# Revit family: ANAESTIVAC 2
name_source: partatom
category: Equipement de génie climatique
revit_build: Autodesk Revit 2018 (Build: 20170223_1515(x64)
units: mm (PartAtom-declared; Revit-internal decimal feet)

## family parameters
Basée sur le plan de construction = Non
Classification = Aucun
Cote de connecteur circulaire = Utiliser le diamètre
Couper avec des vides une fois chargée = Non
Partagée = Non
Point de calcul de pièce = Non
Toujours verticalement = Oui
Type d'élément = Normal

## types (4) — shared parameters
BRANCHEMENT_TERRE = Oui
COFFRET ELEC = COFFRET ELEC STANDARD PM2 : COFFRET MIL 600x300x300
COS_PHI = 0.9
COUPE ASPI LARG = 86.3 mm
DOUBLE_ALIMENTATION = Non
NBR_POLES = 3
NEUTRE = Oui
TENSION_ALIM = 400 V
Zone de maintenance 1 = Oui
Zone de maintenance coffret = Oui
zero-valued in all types: HAUTEUR, LARGEUR, LONGUEUR

## per-type parameters (varying)
| type | CHASSIS_ASPI_LARG | COUPE REFOULEMENT | DEBIT_ASPI_VIDE | DEBIT_REFOUL_VIDE | DEPLACEMENT ASPI DROITE | DEPLACEMENT ASPI GAUCHE | DEPLACEMENT ASPI REOULEMENT HAUTEUR | DEPLACEMENT REFOULEMENT DROITE | DEPLACEMENT REFOULEMENT GAUCHE | DESCR_ALIM_X | DESCR_ASPI | DESCR_REFOUL | DIAM_ASPI_AIR | DIAM_REFOUL_VIDE | NIVEAU_SONORE(dB(A)) | POIDS(Kg) | POMPES | POMPES_LARG | POMPES_LONG | PUISS_APPARENTE | PUISS_ELECT | SUPPORT POMPES |
| Y006V | 58.3 mm | 70 mm  [stored 0.229659 ft] | 150.0 m³/h | 75.0 m³/h | 65 mm  [stored 0.213255 ft] | 165 mm | 288 mm  [stored 0.944882 ft] | 165 mm | 65 mm  [stored 0.213255 ft] | Alimentation électrique, 5G1.5mm² | Aspiration Vide; 150m3/h; G1"1/4"FEM | Refoulement Vide; 75m3/h; Ø44 | 32 mm  [stored 0.104987 ft] | 44 mm  [stored 0.144357 ft] | 61 | 110 mm  [stored 0.360892 ft] | PAV_ANAESTIVAC 2 : Y006V | 572 mm | 199 mm  [stored 0.652887 ft] | 844 VA | 1 kW | SUPPORT ANAESTIVAC 2 : Y006V - Y011V |
| Y011V | 80 mm  [stored 0.262467 ft] | 70 mm  [stored 0.229659 ft] | 288.0 m³/h | 144.0 m³/h | 70 mm  [stored 0.229659 ft] | 185 mm  [stored 0.606955 ft] | 296 mm  [stored 0.971129 ft] | 185 mm  [stored 0.606955 ft] | 70 mm  [stored 0.229659 ft] | Alimentation électrique, 5G2.5mm² | Aspiration Vide; 288m3/h; G1"1/2"FEM | Refoulement Vide; 144m3/h; Ø44 | 40 mm  [stored 0.131234 ft] | 44 mm  [stored 0.144357 ft] | 67 | 120 mm  [stored 0.393701 ft] | PAV_ANAESTIVAC 2 : Y011V | 572 mm | 199 mm  [stored 0.652887 ft] | 2000 VA | 2 kW | SUPPORT ANAESTIVAC 2 : Y006V - Y011V |
| Y020V | 58.3 mm | 90 mm  [stored 0.295276 ft] | 420.0 m³/h | 210.0 m³/h | 87.5 mm  [stored 0.287073 ft] | 207.5 mm  [stored 0.680774 ft] | 298 mm  [stored 0.97769 ft] | 207.5 mm  [stored 0.680774 ft] | 87.5 mm  [stored 0.287073 ft] | Alimentation électrique, 5G4mm² | Aspiration Vide; 420m3/h; G2"FEM | Refoulement Vide; 210m3/h; Ø60 | 50 mm  [stored 0.164042 ft] | 60 mm  [stored 0.19685 ft] | 71 | 140 mm  [stored 0.459318 ft] | PAV_ANAESTIVAC 2 : Y020V | 727 mm  [stored 2.38517 ft] | 225 mm  [stored 0.738189 ft] | 3333 VA | 3 kW | SUPPORT ANAESTIVAC 2 : Y020V - Y030V |
| Y030V | 58.3 mm | 90 mm  [stored 0.295276 ft] | 612.0 m³/h | 306.0 m³/h | 100 mm  [stored 0.328084 ft] | 225 mm  [stored 0.738189 ft] | 303 mm  [stored 0.994094 ft] | 225 mm  [stored 0.738189 ft] | 100 mm  [stored 0.328084 ft] | Alimentation électrique, 5G4mm² | Aspiration Vide; 612m3/h; G2"FEM | Refoulement Vide; 306m3/h; Ø60 | 50 mm  [stored 0.164042 ft] | 60 mm  [stored 0.19685 ft] | 73 | 160 mm  [stored 0.524934 ft] | PAV_ANAESTIVAC 2 : Y030V | 755 mm  [stored 2.47703 ft] | 235 mm | 4889 VA | 4 kW | SUPPORT ANAESTIVAC 2 : Y020V - Y030V |

note: [stored X ft] marks values corroborated as IEEE doubles in the binary element streams (Revit-internal decimal feet)
